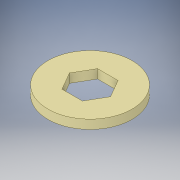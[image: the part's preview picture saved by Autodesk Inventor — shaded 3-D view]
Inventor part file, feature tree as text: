
AUTODESK INVENTOR PART (.ipt)
format: ipt  version: 2019 (Build 230136000, 136)  size: 116,224 bytes
history: native  units: mm
features: other x1, extrude x1, sketch x1
ambient origin geometry x8: Origin, YZ Plane, XZ Plane, XY Plane, X Axis, Y Axis, Z Axis, Center Point
bodies: Body1 (feature_tree)
feature tree (3):
  other  "Sólido1"
  extrude  "Extrusión1"  TaperAngle=0.0deg  [1 undecoded]
  sketch  "Boceto1"  dims[d0=12.7mm d1=0.0mm d2=30.0mm d3=3.18mm d4=0.0mm]
note: 1 required parameter value undecoded (feature->parameter linkage not recoverable at this tier; creation-order binding heuristic only, values carry confidence <= 0.55)
